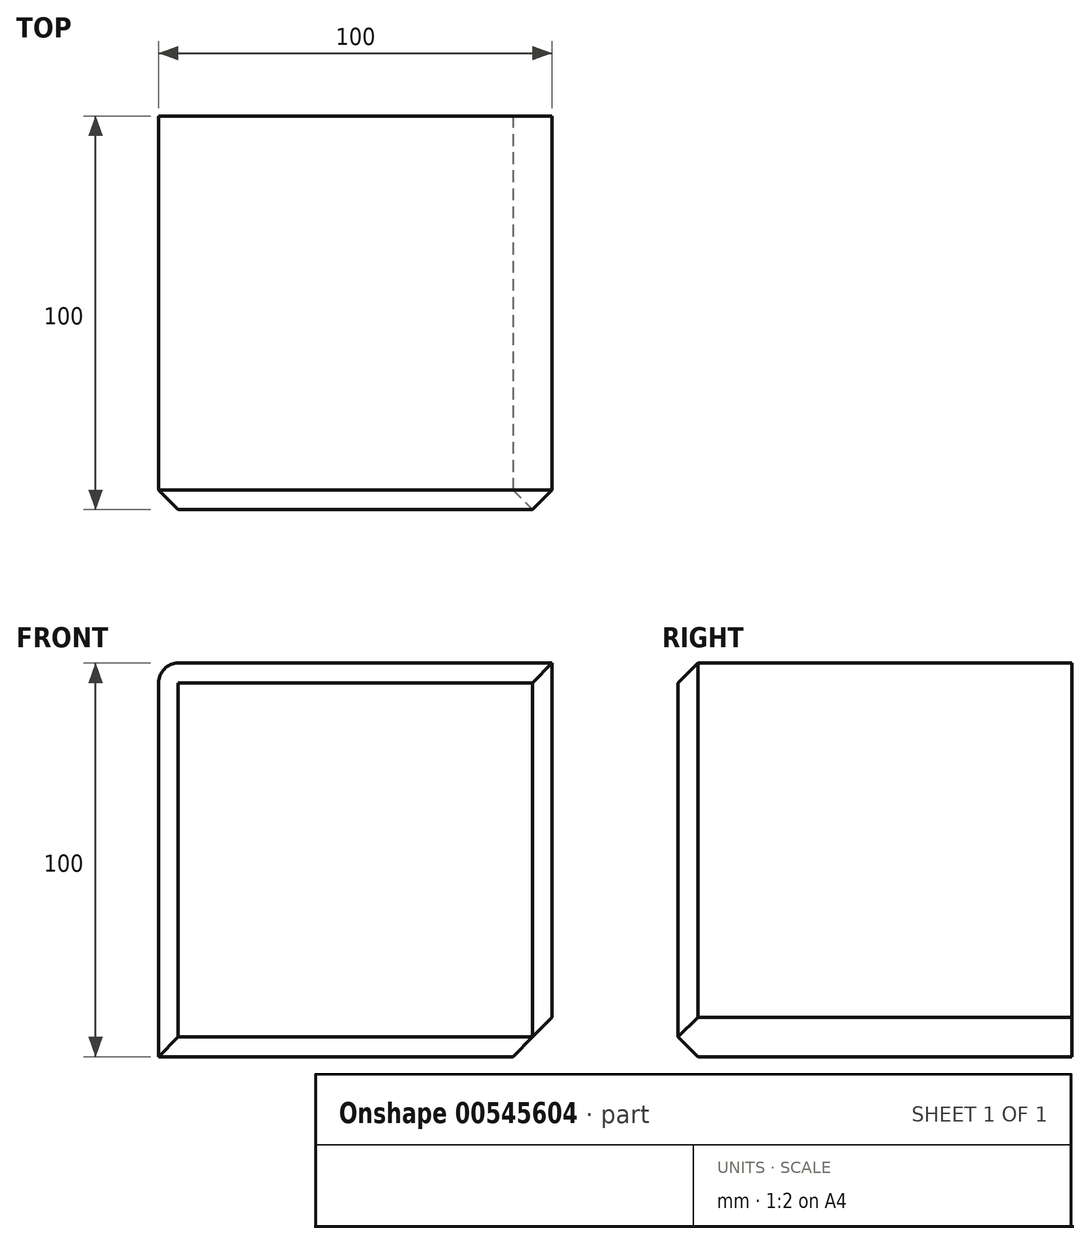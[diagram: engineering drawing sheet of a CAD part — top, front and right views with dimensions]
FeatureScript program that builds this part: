
annotation { "Feature Type Name" : "Feature", "Feature Type Description" : "" }
export const myFeature = defineFeature(function(context is Context, id is Id, definition is map)
    precondition{}
    {
        {
            var Q0;
            Q0=qCreatedBy(makeId("Front.planeOp"),FACE);
            var sketch = newSketch(context, id + "F0", { "sketchPlane" : qUnion([Q0])});
            skLineSegment(sketch, "E0.bottom", {"start": v(-50, 50) * mm, "end": v(50, 50) * mm});
            skLineSegment(sketch, "E0.top", {"start": v(-50, -50) * mm, "end": v(50, -50) * mm});
            skLineSegment(sketch, "E0.left", {"start": v(-50, 50) * mm, "end": v(-50, -50) * mm});
            skLineSegment(sketch, "E0.right", {"start": v(50, 50) * mm, "end": v(50, -50) * mm});
            skSolve(sketch);
        }
        {
            var Q0;
            Q0 = qSketchRegion(id + "F0", true);
            extrude(context, id + "F1", {"entities" : qUnion([Q0]), "depth" : 100 * mm, "offsetDistance" : 25 * mm});
        }
        {
            var Q0;
            Q0=makeQuery(id+"F1.opExtrude","SWEPT_EDGE",EDGE,{"disambiguationData":[OSD([sQuery(id+"F0.wireOp",EDGE,"E0.bottom"),sQuery(id+"F0.wireOp",EDGE,"E0.left")])]});
            fillet(context, id + "F2", {"entities" : qUnion([Q0]), "radius" : 5 * mm, "tangentPropagation" : true, "allowEdgeOverflow" : false});
        }
        {
            var Q0;
            Q0=makeQuery(id+"F1.opExtrude","CAP_EDGE",EDGE,{"disambiguationData":[OSD([sQuery(id+"F0.wireOp",EDGE,"E0.bottom")])],"isStart":false});
            var Q1;
            Q1=makeQuery(id+"F1.opExtrude","CAP_FACE",FACE,{"disambiguationData":[OSD([sQuery(id+"F0.wireOp",EDGE,"E0.bottom"),sQuery(id+"F0.wireOp",EDGE,"E0.top"),sQuery(id+"F0.wireOp",EDGE,"E0.left"),sQuery(id+"F0.wireOp",EDGE,"E0.right")])],"isStart":false});
            chamfer(context, id + "F3", {"entities" : qUnion([Q0, Q1]), "width" : 5 * mm, "tangentPropagation" : true});
        }
        {
            var Q0;
            Q0=makeQuery(id+"F1.opExtrude","SWEPT_EDGE",EDGE,{"disambiguationData":[OSD([sQuery(id+"F0.wireOp",EDGE,"E0.top"),sQuery(id+"F0.wireOp",EDGE,"E0.right")])]});
            chamfer(context, id + "F4", {"entities" : qUnion([Q0]), "width" : 10 * mm, "tangentPropagation" : true});
        }
    });
